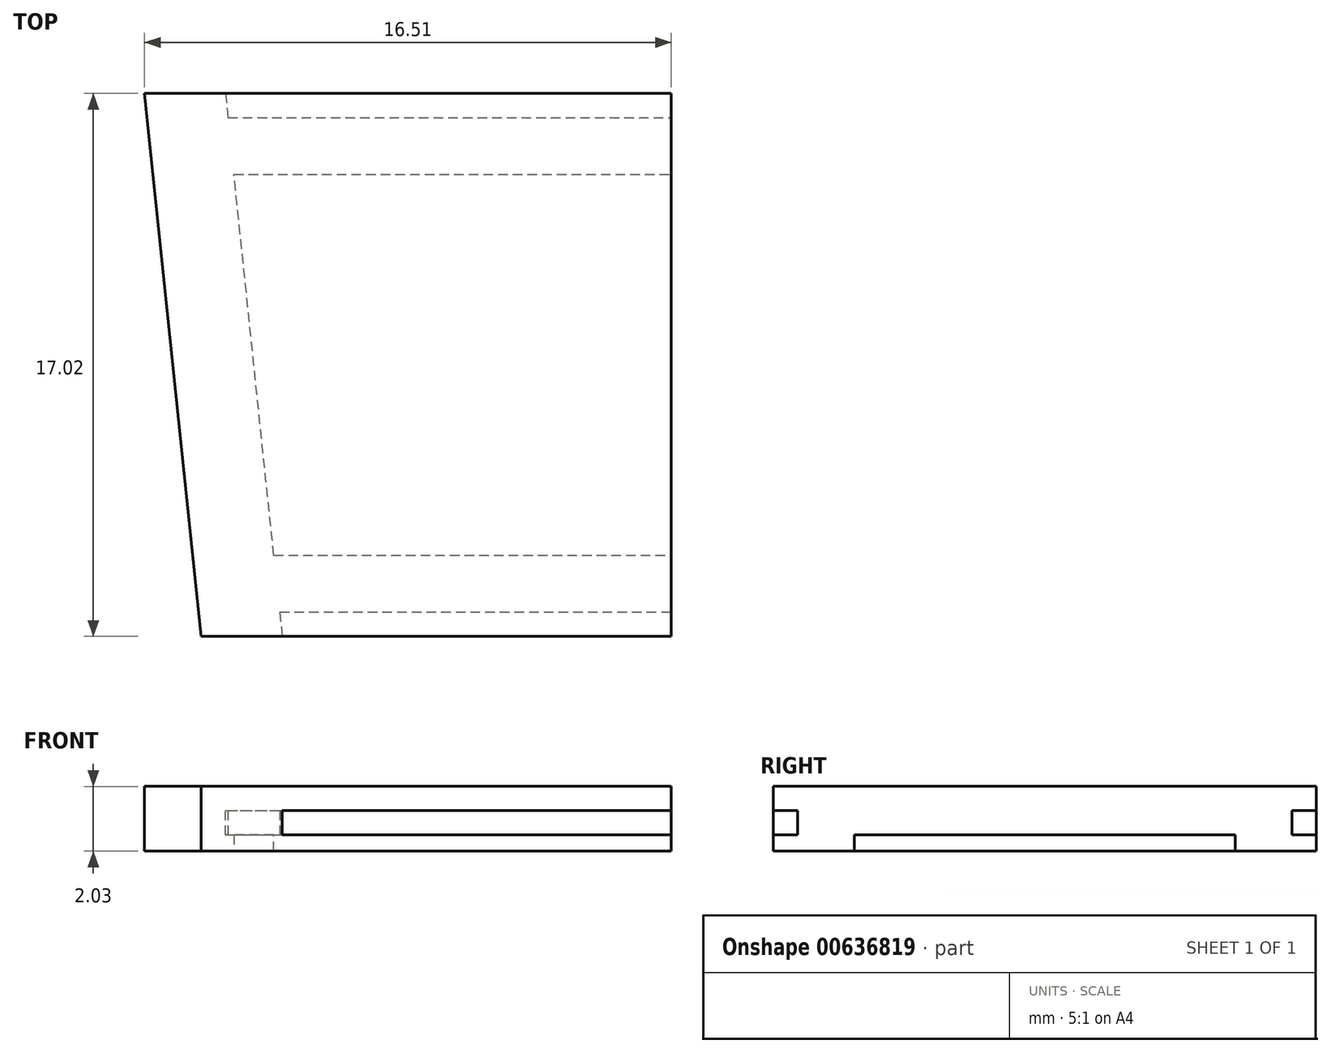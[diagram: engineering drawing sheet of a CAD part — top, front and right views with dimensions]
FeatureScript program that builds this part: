
annotation { "Feature Type Name" : "Feature", "Feature Type Description" : "" }
export const myFeature = defineFeature(function(context is Context, id is Id, definition is map)
    precondition{}
    {
        {
            var Q0;
            Q0=qCreatedBy(makeId("Right.planeOp"),FACE);
            var sketch = newSketch(context, id + "F0", { "sketchPlane" : qUnion([Q0])});
            skLineSegment(sketch, "E0.bottom", {"start": v(0, 0) * mm, "end": v(17.02, 0) * mm});
            skLineSegment(sketch, "E0.top", {"start": v(0, 2.03) * mm, "end": v(17.02, 2.03) * mm});
            skLineSegment(sketch, "E0.left", {"start": v(0, 0) * mm, "end": v(0, 2.03) * mm});
            skLineSegment(sketch, "E0.right", {"start": v(17.02, 0) * mm, "end": v(17.02, 2.03) * mm});
            skSolve(sketch);
        }
        {
            var Q0;
            Q0 = qSketchRegion(id + "F0", true);
            extrude(context, id + "F1", {"entities" : qUnion([Q0]), "depth" : 16.5 * mm, "offsetDistance" : 25.4 * mm});
        }
        {
            var Q0;
            Q0=makeQuery(id+"F1.opExtrude","SWEPT_FACE",FACE,{"disambiguationData":[OSD([sQuery(id+"F0.wireOp",EDGE,"E0.top")])]});
            var sketch = newSketch(context, id + "F2", { "sketchPlane" : qUnion([Q0])});
            skLineSegment(sketch, "E1", {"start": v(0, 17.02) * mm, "end": v(1.78, 0) * mm});
            skSolve(sketch);
        }
        {
            var Q0;
            {var subQ0=sQuery(id+"F2.wireOp",EDGE,"E1");Q0=makeQuery(id+"F2.imprint","IMPRINT",FACE,{"disambiguationData":[TD([[makeQuery(id+"F2.imprint","IMPRINT",EDGE,{"derivedFrom":subQ0}),-1.0]])]});}
            extrude(context, id + "F3", {"entities" : qUnion([Q0]), "operationType" : NewBodyOperationType.REMOVE, "oppositeDirection" : true, "depth" : 25.4 * mm, "offsetDistance" : 25.4 * mm});
        }
        {
            var Q0;
            Q0=makeQuery(id+"F1.opExtrude","CAP_FACE",FACE,{"disambiguationData":[OSD([sQuery(id+"F0.wireOp",EDGE,"E0.bottom"),sQuery(id+"F0.wireOp",EDGE,"E0.top"),sQuery(id+"F0.wireOp",EDGE,"E0.left"),sQuery(id+"F0.wireOp",EDGE,"E0.right")])],"isStart":false});
            var sketch = newSketch(context, id + "F4", { "sketchPlane" : qUnion([Q0])});
            skLineSegment(sketch, "E2", {"start": v(17.02, 1.27) * mm, "end": v(16.26, 1.27) * mm});
            skLineSegment(sketch, "E3", {"start": v(16.26, 1.27) * mm, "end": v(16.26, 0.5) * mm});
            skLineSegment(sketch, "E4", {"start": v(16.26, 0.5) * mm, "end": v(17.02, 0.5) * mm});
            skLineSegment(sketch, "E5", {"start": v(8.5, 0) * mm, "end": v(8.5, 2.03) * mm, "construction": true});
            skLineSegment(sketch, "E6.MirrorCS", {"start": v(0.76, 1.27) * mm, "end": v(0.76, 0.5) * mm});
            skLineSegment(sketch, "E7.MirrorCS", {"start": v(0.76, 0.5) * mm, "end": v(0, 0.5) * mm});
            skLineSegment(sketch, "E8.MirrorCS", {"start": v(0, 1.27) * mm, "end": v(0.76, 1.27) * mm});
            skLineSegment(sketch, "E9", {"start": v(2.54, 0) * mm, "end": v(2.54, 0.5) * mm});
            skLineSegment(sketch, "E10", {"start": v(2.54, 0.5) * mm, "end": v(14.48, 0.5) * mm});
            skLineSegment(sketch, "E11", {"start": v(14.48, 0.5) * mm, "end": v(14.48, 0) * mm});
            skSolve(sketch);
        }
        {
            var Q0;
            Q0=makeQuery(id+"F4.imprint","IMPRINT",FACE,{"disambiguationData":[TD([[makeQuery(id+"F4.imprint","IMPRINT",EDGE,{"derivedFrom":sQuery(id+"F4.wireOp",EDGE,"E6.MirrorCS")}),-1.0]])]});
            var Q1;
            {var subQ0=sQuery(id+"F4.wireOp",EDGE,"E2");Q1=makeQuery(id+"F4.imprint","IMPRINT",FACE,{"disambiguationData":[TD([[makeQuery(id+"F4.imprint","IMPRINT",EDGE,{"derivedFrom":subQ0}),1.0]])]});}
            var Q2;
            {var subQ0=sQuery(id+"F4.wireOp",EDGE,"E9");Q2=makeQuery(id+"F4.imprint","IMPRINT",FACE,{"disambiguationData":[TD([[makeQuery(id+"F4.imprint","IMPRINT",EDGE,{"derivedFrom":subQ0}),-1.0]])]});}
            var Q3;
            Q3=makeQuery(id+"F3.boolean.opBoolean","COPY",FACE,{"derivedFrom":makeQuery(id+"F3.opExtrude","SWEPT_FACE",FACE,{"disambiguationData":[OSD([sQuery(id+"F2.wireOp",EDGE,"E1")])]})});
            extrude(context, id + "F5", {"entities" : qUnion([Q0, Q1, Q2]), "operationType" : NewBodyOperationType.REMOVE, "endBound" : BoundingType.UP_TO_SURFACE, "oppositeDirection" : true, "depth" : 25.4 * mm, "endBoundEntityFace" : qUnion([Q3]), "hasOffset" : true, "offsetDistance" : 2.54 * mm});
        }
    });
